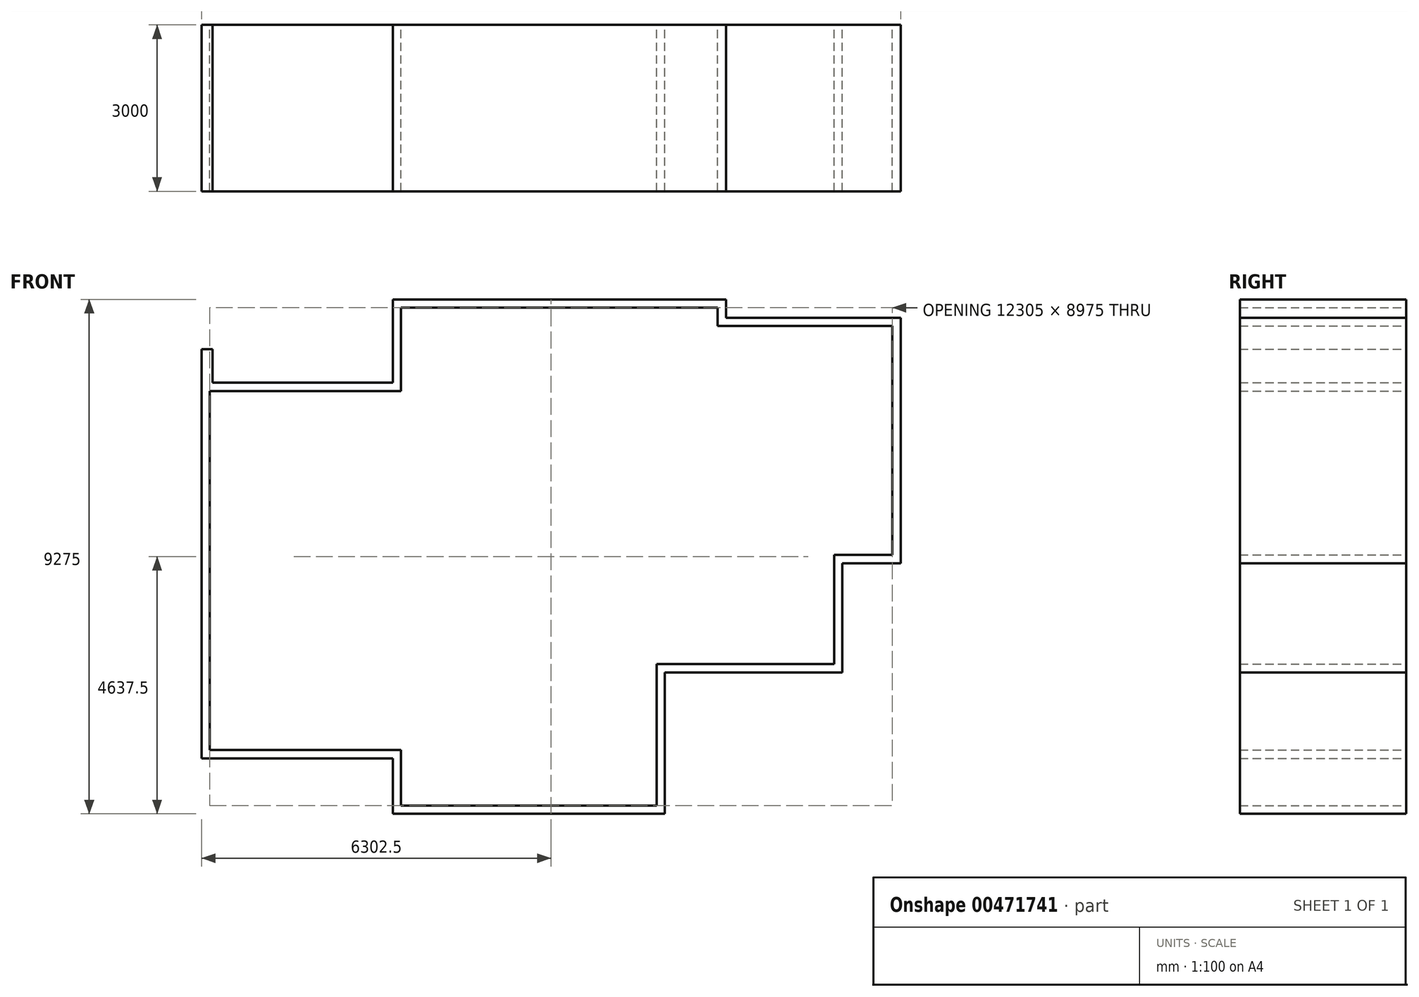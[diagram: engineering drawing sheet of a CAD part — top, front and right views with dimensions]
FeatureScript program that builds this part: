
annotation { "Feature Type Name" : "Feature", "Feature Type Description" : "" }
export const myFeature = defineFeature(function(context is Context, id is Id, definition is map)
    precondition{}
    {
        {
            var Q0;
            Q0=qCreatedBy(makeId("Front.planeOp"),FACE);
            var sketch = newSketch(context, id + "F0", { "sketchPlane" : qUnion([Q0])});
            skLineSegment(sketch, "E0", {"start": v(821.64, -3520) * mm, "end": v(821.64, -720) * mm});
            skLineSegment(sketch, "E1", {"start": v(821.64, -720) * mm, "end": v(821.64, 3255) * mm});
            skLineSegment(sketch, "E2", {"start": v(821.64, 3255) * mm, "end": v(821.64, 3855) * mm});
            skLineSegment(sketch, "E3", {"start": v(821.64, 3855) * mm, "end": v(1021.64, 3855) * mm});
            skLineSegment(sketch, "E4", {"start": v(1021.64, 3855) * mm, "end": v(1021.64, 3255) * mm});
            skLineSegment(sketch, "E5", {"start": v(1021.64, 3255) * mm, "end": v(4271.64, 3255) * mm});
            skLineSegment(sketch, "E6", {"start": v(4271.64, 3255) * mm, "end": v(4271.64, 4755) * mm});
            skLineSegment(sketch, "E7", {"start": v(4271.64, 4755) * mm, "end": v(7326.64, 4755) * mm});
            skLineSegment(sketch, "E8", {"start": v(7326.64, 4755) * mm, "end": v(10276.64, 4755) * mm});
            skLineSegment(sketch, "E9", {"start": v(10276.64, 4755) * mm, "end": v(10276.64, 4425) * mm});
            skLineSegment(sketch, "E10", {"start": v(10276.64, 4425) * mm, "end": v(13426.64, 4425) * mm});
            skLineSegment(sketch, "E11", {"start": v(13426.64, 4425) * mm, "end": v(13426.64, 0) * mm});
            skLineSegment(sketch, "E12", {"start": v(13426.64, 0) * mm, "end": v(12376.64, 0) * mm});
            skLineSegment(sketch, "E13", {"start": v(12376.64, 0) * mm, "end": v(12376.64, -1970) * mm});
            skLineSegment(sketch, "E14", {"start": v(12376.64, -1970) * mm, "end": v(9176.64, -1970) * mm});
            skLineSegment(sketch, "E15", {"start": v(9176.64, -1970) * mm, "end": v(9176.64, -4520) * mm});
            skLineSegment(sketch, "E16", {"start": v(9176.64, -4520) * mm, "end": v(7726.64, -4520) * mm});
            skLineSegment(sketch, "E17", {"start": v(7726.64, -4520) * mm, "end": v(4271.64, -4520) * mm});
            skLineSegment(sketch, "E18", {"start": v(4271.64, -4520) * mm, "end": v(4271.64, -3520) * mm});
            skLineSegment(sketch, "E19", {"start": v(4271.64, -3520) * mm, "end": v(2571.64, -3520) * mm});
            skLineSegment(sketch, "E20", {"start": v(2571.64, -3520) * mm, "end": v(821.64, -3520) * mm});
            skLineSegment(sketch, "E21.0", {"start": v(10126.64, 4605) * mm, "end": v(10126.64, 4275) * mm});
            skLineSegment(sketch, "E21.1", {"start": v(7326.64, 4605) * mm, "end": v(10126.64, 4605) * mm});
            skLineSegment(sketch, "E21.2", {"start": v(4421.64, 4605) * mm, "end": v(7326.64, 4605) * mm});
            skLineSegment(sketch, "E21.3", {"start": v(4421.64, 3105) * mm, "end": v(4421.64, 4605) * mm});
            skLineSegment(sketch, "E21.4", {"start": v(971.64, 3105) * mm, "end": v(4421.64, 3105) * mm});
            skLineSegment(sketch, "E21.5", {"start": v(10126.64, 4275) * mm, "end": v(13276.64, 4275) * mm});
            skLineSegment(sketch, "E21.9", {"start": v(971.64, -720) * mm, "end": v(971.64, 3105) * mm});
            skLineSegment(sketch, "E21.10", {"start": v(971.64, -3370) * mm, "end": v(971.64, -720) * mm});
            skLineSegment(sketch, "E21.11", {"start": v(12226.64, -1820) * mm, "end": v(9026.64, -1820) * mm});
            skLineSegment(sketch, "E21.12", {"start": v(12226.64, 150) * mm, "end": v(12226.64, -1820) * mm});
            skLineSegment(sketch, "E21.13", {"start": v(13276.64, 150) * mm, "end": v(12226.64, 150) * mm});
            skLineSegment(sketch, "E21.14", {"start": v(13276.64, 4275) * mm, "end": v(13276.64, 150) * mm});
            skLineSegment(sketch, "E21.15", {"start": v(9026.64, -1820) * mm, "end": v(9026.64, -4370) * mm});
            skLineSegment(sketch, "E21.16", {"start": v(9026.64, -4370) * mm, "end": v(7726.64, -4370) * mm});
            skLineSegment(sketch, "E21.17", {"start": v(7726.64, -4370) * mm, "end": v(4421.64, -4370) * mm});
            skLineSegment(sketch, "E21.18", {"start": v(4421.64, -4370) * mm, "end": v(4421.64, -3370) * mm});
            skLineSegment(sketch, "E21.19", {"start": v(4421.64, -3370) * mm, "end": v(2571.64, -3370) * mm});
            skLineSegment(sketch, "E21.20", {"start": v(2571.64, -3370) * mm, "end": v(971.64, -3370) * mm});
            skLineSegment(sketch, "E22.filletArc", {"start": v(971.64, 3105) * mm, "end": v(971.64, 3105) * mm});
            skSolve(sketch);
        }
        {
            var Q0;
            Q0=makeQuery(id+"F0.imprint","IMPRINT",FACE,{"disambiguationData":[TD([[makeQuery(id+"F0.imprint","IMPRINT",EDGE,{"derivedFrom":sQuery(id+"F0.wireOp",EDGE,"E0")}),-1.0]])]});
            extrude(context, id + "F1", {"entities" : qUnion([Q0]), "depth" : 3000 * mm});
        }
    });
